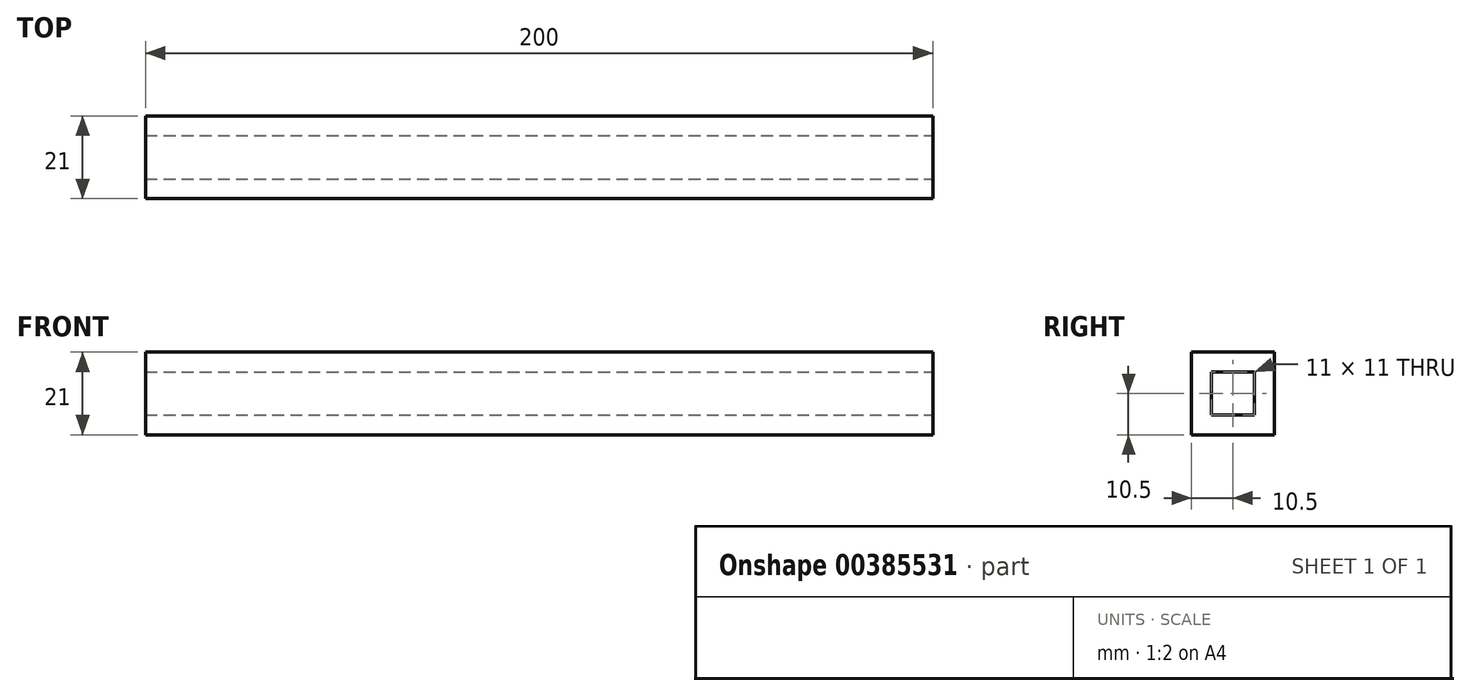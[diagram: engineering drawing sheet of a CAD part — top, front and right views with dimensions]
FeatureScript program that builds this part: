
annotation { "Feature Type Name" : "Feature", "Feature Type Description" : "" }
export const myFeature = defineFeature(function(context is Context, id is Id, definition is map)
    precondition{}
    {
        {
            var Q0;
            Q0=qCreatedBy(makeId("Front.planeOp"),FACE);
            var sketch = newSketch(context, id + "F0", { "sketchPlane" : qUnion([Q0])});
            skLineSegment(sketch, "E0.bottom", {"start": v(0, 0) * mm, "end": v(-200, 0) * mm});
            skLineSegment(sketch, "E0.top", {"start": v(0, 21) * mm, "end": v(-200, 21) * mm});
            skLineSegment(sketch, "E0.left", {"start": v(0, 0) * mm, "end": v(0, 21) * mm});
            skLineSegment(sketch, "E0.right", {"start": v(-200, 0) * mm, "end": v(-200, 21) * mm});
            skSolve(sketch);
        }
        {
            var Q0;
            Q0 = qSketchRegion(id + "F0", true);
            extrude(context, id + "F1", {"entities" : qUnion([Q0]), "depth" : 21 * mm});
        }
        {
            var Q0;
            Q0=qCreatedBy(makeId("Right.planeOp"),FACE);
            var sketch = newSketch(context, id + "F2", { "sketchPlane" : qUnion([Q0])});
            skLineSegment(sketch, "E1.0", {"start": v(-5, 5) * mm, "end": v(-5, 16) * mm});
            skLineSegment(sketch, "E1.1", {"start": v(-16, 5) * mm, "end": v(-5, 5) * mm});
            skLineSegment(sketch, "E1.2", {"start": v(-16, 16) * mm, "end": v(-16, 5) * mm});
            skLineSegment(sketch, "E1.3", {"start": v(-5, 16) * mm, "end": v(-16, 16) * mm});
            skSolve(sketch);
        }
        {
            var Q0;
            Q0=makeQuery(id+"F2.imprint","IMPRINT",FACE,{"disambiguationData":[TD([[makeQuery(id+"F2.imprint","IMPRINT",EDGE,{"derivedFrom":sQuery(id+"F2.wireOp",EDGE,"E1.0")}),1.0]])]});
            extrude(context, id + "F3", {"entities" : qUnion([Q0]), "operationType" : NewBodyOperationType.REMOVE, "oppositeDirection" : true, "depth" : 200 * mm});
        }
    });
